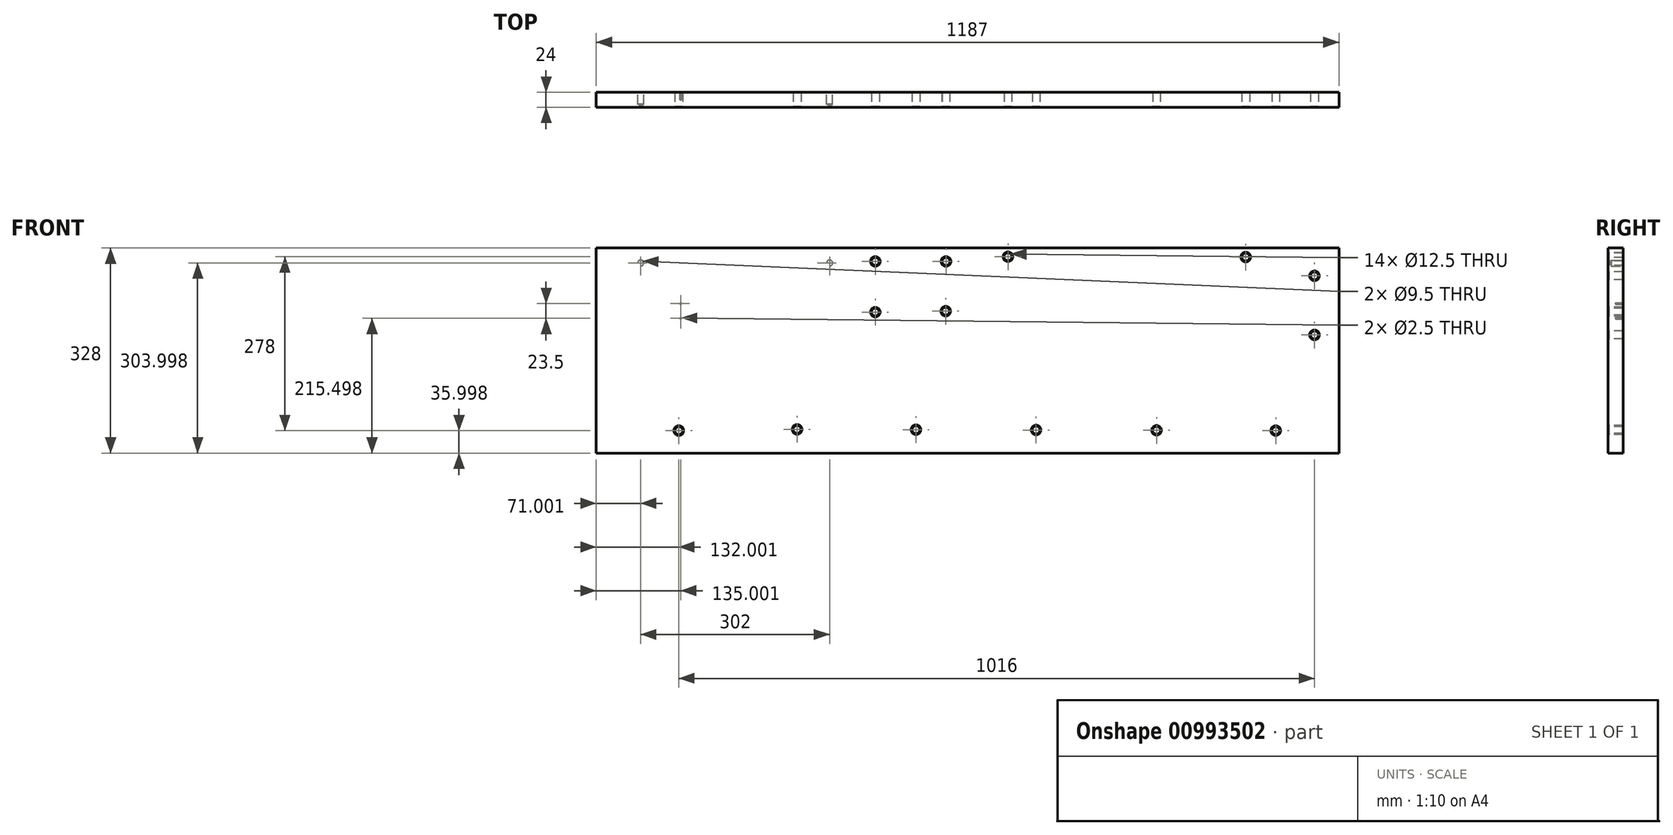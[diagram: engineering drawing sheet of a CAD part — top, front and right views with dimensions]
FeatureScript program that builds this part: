
annotation { "Feature Type Name" : "Feature", "Feature Type Description" : "" }
export const myFeature = defineFeature(function(context is Context, id is Id, definition is map)
    precondition{}
    {
        {
            var Q0;
            Q0=qCreatedBy(makeId("Front.planeOp"),FACE);
            var sketch = newSketch(context, id + "F0", { "sketchPlane" : qUnion([Q0])});
            skLineSegment(sketch, "E0.bottom", {"start": v(-97.8, 337.24) * mm, "end": v(1089.2, 337.24) * mm});
            skLineSegment(sketch, "E0.top", {"start": v(-97.8, 9.24) * mm, "end": v(1089.2, 9.24) * mm});
            skLineSegment(sketch, "E0.left", {"start": v(-97.8, 337.24) * mm, "end": v(-97.8, 9.24) * mm});
            skLineSegment(sketch, "E0.right", {"start": v(1089.2, 337.24) * mm, "end": v(1089.2, 9.24) * mm});
            skPoint(sketch, "E1", {"position": v(348.2, 315.74) * mm});
            skPoint(sketch, "E2", {"position": v(461.2, 315.74) * mm});
            skPoint(sketch, "E3", {"position": v(460.7, 236.24) * mm});
            skPoint(sketch, "E4", {"position": v(348.2, 234.74) * mm});
            skPoint(sketch, "E5", {"position": v(560.2, 323.24) * mm});
            skPoint(sketch, "E6", {"position": v(940.2, 322.74) * mm});
            skPoint(sketch, "E7", {"position": v(1050.2, 292.74) * mm});
            skPoint(sketch, "E8", {"position": v(1050.2, 198.24) * mm});
            skPoint(sketch, "E9", {"position": v(34.2, 45.24) * mm});
            skPoint(sketch, "E10", {"position": v(223.2, 47.24) * mm});
            skPoint(sketch, "E11", {"position": v(413.2, 46.74) * mm});
            skPoint(sketch, "E12", {"position": v(605.2, 46.24) * mm});
            skPoint(sketch, "E13", {"position": v(797.7, 45.74) * mm});
            skPoint(sketch, "E14", {"position": v(988.2, 45.24) * mm});
            skSolve(sketch);
        }
        {
            var Q0;
            Q0=makeQuery(id+"F0.imprint","IMPRINT",FACE,{"disambiguationData":[TD([[makeQuery(id+"F0.imprint","IMPRINT",EDGE,{"derivedFrom":sQuery(id+"F0.wireOp",EDGE,"E0.bottom")}),-1.0]])]});
            extrude(context, id + "F1", {"entities" : qUnion([Q0]), "oppositeDirection" : true, "depth" : 24 * mm, "offsetDistance" : 25 * mm});
        }
        {
            var Q0;
            Q0=sQuery(id+"F0.wireOp",VERTEX,"E1");
            var Q1;
            Q1=sQuery(id+"F0.wireOp",VERTEX,"E2");
            var Q2;
            Q2=sQuery(id+"F0.wireOp",VERTEX,"E4");
            var Q3;
            Q3=sQuery(id+"F0.wireOp",VERTEX,"E3");
            var Q4;
            Q4=sQuery(id+"F0.wireOp",VERTEX,"E5");
            var Q5;
            Q5=sQuery(id+"F0.wireOp",VERTEX,"E6");
            var Q6;
            Q6=sQuery(id+"F0.wireOp",VERTEX,"E7");
            var Q7;
            Q7=sQuery(id+"F0.wireOp",VERTEX,"E8");
            var Q8;
            Q8=sQuery(id+"F0.wireOp",VERTEX,"E14");
            var Q9;
            Q9=sQuery(id+"F0.wireOp",VERTEX,"E13");
            var Q10;
            Q10=sQuery(id+"F0.wireOp",VERTEX,"E12");
            var Q11;
            Q11=sQuery(id+"F0.wireOp",VERTEX,"E11");
            var Q12;
            Q12=sQuery(id+"F0.wireOp",VERTEX,"E10");
            var Q13;
            Q13=sQuery(id+"F0.wireOp",VERTEX,"E9");
            var Q14;
            Q14=makeQuery(id+"F1.opExtrude","SWEPT_BODY",BODY,{"disambiguationData":[OSD([sQuery(id+"F0.wireOp",EDGE,"E0.bottom"),sQuery(id+"F0.wireOp",EDGE,"E0.top"),sQuery(id+"F0.wireOp",EDGE,"E0.left"),sQuery(id+"F0.wireOp",EDGE,"E0.right")])]});
            hole(context, id + "F2", {"style" : HoleStyle.C_SINK, "endStyle" : HoleEndStyle.THROUGH, "holeDiameter" : 12.5 * mm, "cSinkDiameter" : 15.5 * mm, "cSinkAngle" : 90 * degree, "majorDiameter" : 5 * mm, "isTappedThrough" : true, "tappedDepth" : 12 * mm, "tapClearance" : 3, "locations" : qUnion([Q0, Q1, Q2, Q3, Q4, Q5, Q6, Q7, Q8, Q9, Q10, Q11, Q12, Q13]), "scope" : qUnion([Q14])});
        }
        {
            var Q0;
            Q0=makeQuery(id+"F1.opExtrude","CAP_FACE",FACE,{"disambiguationData":[OSD([sQuery(id+"F0.wireOp",EDGE,"E0.bottom"),sQuery(id+"F0.wireOp",EDGE,"E0.top"),sQuery(id+"F0.wireOp",EDGE,"E0.left"),sQuery(id+"F0.wireOp",EDGE,"E0.right")])],"isStart":false});
            var sketch = newSketch(context, id + "F3", { "sketchPlane" : qUnion([Q0])});
            skPoint(sketch, "E15", {"position": v(26.8, 313.24) * mm});
            skPoint(sketch, "E16", {"position": v(-275.2, 313.24) * mm});
            skPoint(sketch, "E17", {"position": v(-37.2, 248.24) * mm});
            skPoint(sketch, "E18", {"position": v(-37.2, 224.74) * mm});
            skSolve(sketch);
        }
        {
            var Q0;
            Q0=sQuery(id+"F3.wireOp",VERTEX,"E16");
            var Q1;
            Q1=sQuery(id+"F3.wireOp",VERTEX,"E15");
            var Q2;
            Q2=makeQuery(id+"F1.opExtrude","SWEPT_BODY",BODY,{"disambiguationData":[OSD([sQuery(id+"F0.wireOp",EDGE,"E0.bottom"),sQuery(id+"F0.wireOp",EDGE,"E0.top"),sQuery(id+"F0.wireOp",EDGE,"E0.left"),sQuery(id+"F0.wireOp",EDGE,"E0.right")])]});
            hole(context, id + "F4", {"style" : HoleStyle.SIMPLE, "endStyle" : HoleEndStyle.BLIND, "holeDiameter" : 9.5 * mm, "majorDiameter" : 5 * mm, "holeDepth" : 19 * mm, "isTappedThrough" : true, "tappedDepth" : 12 * mm, "tapClearance" : 3, "locations" : qUnion([Q0, Q1]), "scope" : qUnion([Q2])});
        }
        {
            var Q0;
            Q0=sQuery(id+"F3.wireOp",VERTEX,"E17");
            var Q1;
            Q1=sQuery(id+"F3.wireOp",VERTEX,"E18");
            var Q2;
            Q2=makeQuery(id+"F1.opExtrude","SWEPT_BODY",BODY,{"disambiguationData":[OSD([sQuery(id+"F0.wireOp",EDGE,"E0.bottom"),sQuery(id+"F0.wireOp",EDGE,"E0.top"),sQuery(id+"F0.wireOp",EDGE,"E0.left"),sQuery(id+"F0.wireOp",EDGE,"E0.right")])]});
            hole(context, id + "F5", {"style" : HoleStyle.SIMPLE, "endStyle" : HoleEndStyle.BLIND, "holeDiameter" : 2.5 * mm, "majorDiameter" : 5 * mm, "holeDepth" : 12 * mm, "isTappedThrough" : true, "tappedDepth" : 12 * mm, "tapClearance" : 3, "locations" : qUnion([Q0, Q1]), "scope" : qUnion([Q2])});
        }
    });
